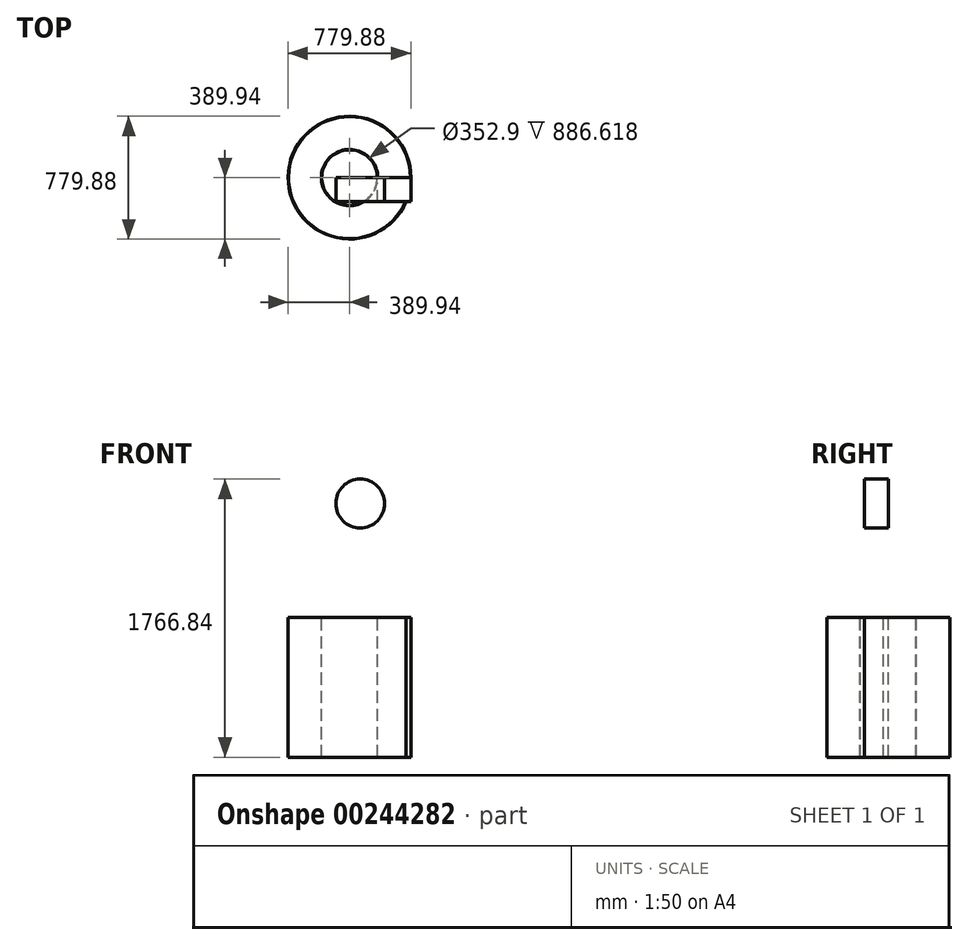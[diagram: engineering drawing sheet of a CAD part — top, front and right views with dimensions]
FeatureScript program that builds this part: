
annotation { "Feature Type Name" : "Feature", "Feature Type Description" : "" }
export const myFeature = defineFeature(function(context is Context, id is Id, definition is map)
    precondition{}
    {
        {
            var Q0;
            Q0=qCreatedBy(makeId("Front.planeOp"),FACE);
            var sketch = newSketch(context, id + "F0", { "sketchPlane" : qUnion([Q0])});
            skLineSegment(sketch, "E0", {"start": v(0, 731.95) * mm, "end": v(0, -740.66) * mm});
            skLineSegment(sketch, "E1.bottom", {"start": v(176.45, 461.83) * mm, "end": v(389.94, 461.83) * mm});
            skLineSegment(sketch, "E1.top", {"start": v(176.45, -424.8) * mm, "end": v(389.94, -424.8) * mm});
            skLineSegment(sketch, "E1.left", {"start": v(176.45, 461.83) * mm, "end": v(176.45, -424.8) * mm});
            skLineSegment(sketch, "E1.right", {"start": v(389.94, 461.83) * mm, "end": v(389.94, -424.8) * mm});
            skCircle(sketch, "E2", {"center": v(68.22, 1187) * mm, "radius": 155.05 * mm});
            skSolve(sketch);
        }
        {
            var Q0;
            Q0=makeQuery(id+"F0.imprint","IMPRINT",FACE,{"disambiguationData":[TD([[makeQuery(id+"F0.imprint","IMPRINT",EDGE,{"derivedFrom":sQuery(id+"F0.wireOp",EDGE,"E1.bottom")}),-1.0]])]});
            var Q1;
            Q1=sQuery(id+"F0.wireOp",EDGE,"E0");
            revolve(context, id + "F1", {"entities" : qUnion([Q0]), "axis" : qUnion([Q1]), "revolveType" : RevolveType.FULL});
        }
        {
            var Q0;
            Q0=makeQuery(id+"F1.opRevolve","SWEPT_FACE",FACE,{"disambiguationData":[OSD([sQuery(id+"F0.wireOp",EDGE,"E1.bottom")])]});
            shell(context, id + "F2", {"entities" : qUnion([Q0]), "thickness" : 2.54 * mm});
        }
        {
            var Q0;
            Q0 = qSketchRegion(id + "F0", true);
            extrude(context, id + "F3", {"entities" : qUnion([Q0]), "operationType" : NewBodyOperationType.ADD, "depth" : 152.4 * mm});
        }
    });
